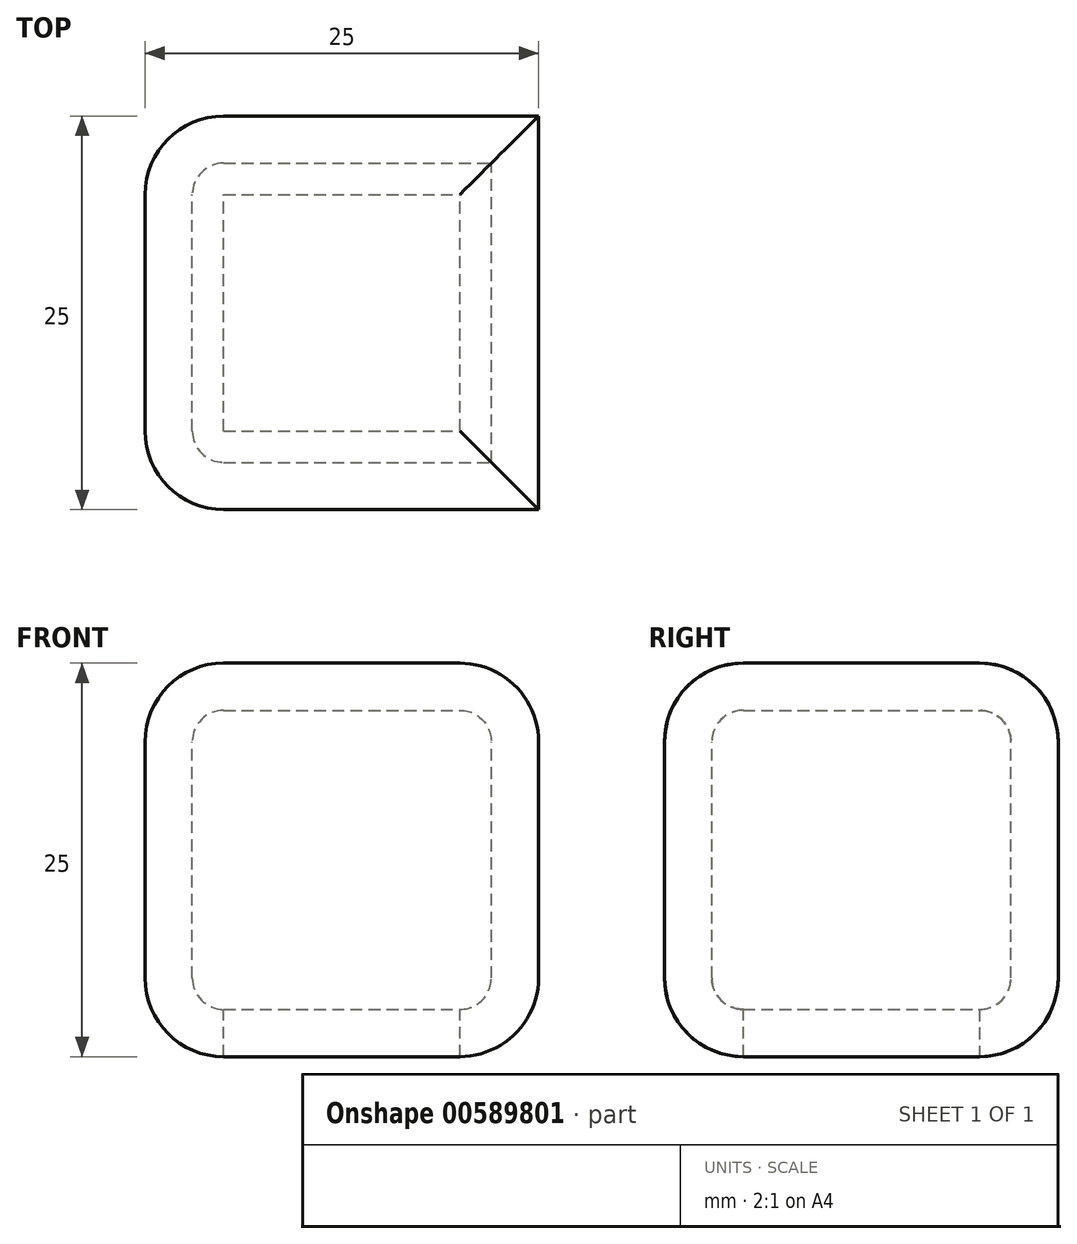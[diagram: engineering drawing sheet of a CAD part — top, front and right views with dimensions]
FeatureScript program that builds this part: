
annotation { "Feature Type Name" : "Feature", "Feature Type Description" : "" }
export const myFeature = defineFeature(function(context is Context, id is Id, definition is map)
    precondition{}
    {
        {
            var Q0;
            Q0=qCreatedBy(makeId("Front.planeOp"),FACE);
            var sketch = newSketch(context, id + "F0", { "sketchPlane" : qUnion([Q0])});
            skLineSegment(sketch, "E0.bottom", {"start": v(0, 0) * mm, "end": v(25, 0) * mm});
            skLineSegment(sketch, "E0.top", {"start": v(0, 25) * mm, "end": v(25, 25) * mm});
            skLineSegment(sketch, "E0.left", {"start": v(0, 0) * mm, "end": v(0, 25) * mm});
            skLineSegment(sketch, "E0.right", {"start": v(25, 0) * mm, "end": v(25, 25) * mm});
            skSolve(sketch);
        }
        {
            var Q0;
            Q0=makeQuery(id+"F0.imprint","IMPRINT",FACE,{"disambiguationData":[TD([[makeQuery(id+"F0.imprint","IMPRINT",EDGE,{"derivedFrom":sQuery(id+"F0.wireOp",EDGE,"E0.bottom")}),1.0]])]});
            extrude(context, id + "F1", {"entities" : qUnion([Q0]), "depth" : 25 * mm, "offsetDistance" : 25 * mm});
        }
        {
            var Q0;
            Q0=makeQuery(id+"F1.opExtrude","CAP_EDGE",EDGE,{"disambiguationData":[OSD([sQuery(id+"F0.wireOp",EDGE,"E0.bottom")])],"isStart":true});
            var Q1;
            Q1=makeQuery(id+"F1.opExtrude","SWEPT_EDGE",EDGE,{"disambiguationData":[OSD([sQuery(id+"F0.wireOp",EDGE,"E0.bottom"),sQuery(id+"F0.wireOp",EDGE,"E0.right")])]});
            var Q2;
            Q2=makeQuery(id+"F1.opExtrude","SWEPT_EDGE",EDGE,{"disambiguationData":[OSD([sQuery(id+"F0.wireOp",EDGE,"E0.top"),sQuery(id+"F0.wireOp",EDGE,"E0.right")])]});
            var Q3;
            Q3=makeQuery(id+"F1.opExtrude","CAP_EDGE",EDGE,{"disambiguationData":[OSD([sQuery(id+"F0.wireOp",EDGE,"E0.top")])],"isStart":true});
            var Q4;
            Q4=makeQuery(id+"F1.opExtrude","CAP_EDGE",EDGE,{"disambiguationData":[OSD([sQuery(id+"F0.wireOp",EDGE,"E0.top")])],"isStart":false});
            var Q5;
            Q5=makeQuery(id+"F1.opExtrude","SWEPT_EDGE",EDGE,{"disambiguationData":[OSD([sQuery(id+"F0.wireOp",EDGE,"E0.top"),sQuery(id+"F0.wireOp",EDGE,"E0.left")])]});
            var Q6;
            Q6=makeQuery(id+"F1.opExtrude","CAP_EDGE",EDGE,{"disambiguationData":[OSD([sQuery(id+"F0.wireOp",EDGE,"E0.bottom")])],"isStart":false});
            var Q7;
            Q7=makeQuery(id+"F1.opExtrude","CAP_EDGE",EDGE,{"disambiguationData":[OSD([sQuery(id+"F0.wireOp",EDGE,"E0.left")])],"isStart":false});
            var Q8;
            Q8=makeQuery(id+"F1.opExtrude","CAP_EDGE",EDGE,{"disambiguationData":[OSD([sQuery(id+"F0.wireOp",EDGE,"E0.left")])],"isStart":true});
            var Q9;
            Q9=makeQuery(id+"F1.opExtrude","SWEPT_EDGE",EDGE,{"disambiguationData":[OSD([sQuery(id+"F0.wireOp",EDGE,"E0.bottom"),sQuery(id+"F0.wireOp",EDGE,"E0.left")])]});
            fillet(context, id + "F2", {"entities" : qUnion([Q0, Q1, Q2, Q3, Q4, Q5, Q6, Q7, Q8, Q9]), "radius" : 5 * mm, "tangentPropagation" : true, "allowEdgeOverflow" : false});
        }
        {
            var Q0;
            Q0=makeQuery(id+"F1.opExtrude","SWEPT_FACE",FACE,{"disambiguationData":[OSD([sQuery(id+"F0.wireOp",EDGE,"E0.bottom")])]});
            shell(context, id + "F3", {"entities" : qUnion([Q0]), "thickness" : 3 * mm});
        }
    });
